# Revit family: Burko F-9000 Pendel
name_source: partatom
category: HLS-Bauteile
units: mm (PartAtom-declared; Revit-internal decimal feet)

## family parameters
Arbeitsebenenbasiert = Nein
Beim Laden mit Abzugskörper schneiden = Nein
Bemaßung runder Anschluss = Durchmesser verwenden
Beschriftungsausrichtung beibehalten = Nein
Gemeinsam genutzt = Nein
Immer vertikal = Ja
Klassifizierung = Keine
Raumberechnungspunkt = Nein
Teiletyp = Normal

## types (5) — shared parameters
Anschluss 1" = 25 mm  [stored 0.082021 ft]
Anschluss 1/2" = 15 mm  [stored 0.0492126 ft]
Datenblatt = https://www.burkhalter-h2o.ch
Homepage = https://www.burkhalter-h2o.ch
LUT = LUT_Burko_F-9000
Sockel_Höhe = 100 mm  [stored 0.328084 ft]
Steuerung_Breite = 200 mm  [stored 0.656168 ft]
Steuerung_Höhe = 175 mm  [stored 0.574147 ft]
Steuerung_Tiefe = 75 mm  [stored 0.246063 ft]
zero-valued in all types: Vorgabe-Ansicht

## per-type parameters (varying)
| type | A | B | Behälterkopf | C | G | Harzinhalt_pro_Harzdruckbehälter | Sockel_Absatz_Oben | Sockel_Absatz_Unten |
| Burko F-9000 - 15L | 208 mm | 940 mm  [stored 3.08399 ft] | 75 mm  [stored 0.246063 ft] | 1070 mm  [stored 3.5105 ft] | 370 mm  [stored 1.21391 ft] | 15L | 84 mm  [stored 0.275591 ft] | 114 mm  [stored 0.374016 ft] |
| Burko F-9000 - 25L | 257 mm  [stored 0.843176 ft] | 940 mm  [stored 3.08399 ft] | 100 mm  [stored 0.328084 ft] | 1070 mm  [stored 3.5105 ft] | 450 mm  [stored 1.47638 ft] | 25L | 109 mm  [stored 0.357612 ft] | 139 mm  [stored 0.456037 ft] |
| Burko F-9000 - 50L | 304 mm  [stored 0.997375 ft] | 1270 mm  [stored 4.16667 ft] | 125 mm  [stored 0.410105 ft] | 1400 mm  [stored 4.59318 ft] | 450 mm  [stored 1.47638 ft] | 50L | 132 mm  [stored 0.433071 ft] | 162 mm  [stored 0.531496 ft] |
| Burko F-9000 - 75L | 369 mm  [stored 1.21063 ft] | 1710 mm  [stored 5.61024 ft] | 125 mm  [stored 0.410105 ft] | 1840 mm  [stored 6.03675 ft] | 650 mm  [stored 2.13255 ft] | 75L | 165 mm | 195 mm  [stored 0.639764 ft] |
| Burko F-9000 - 100L | 406 mm  [stored 1.33202 ft] | 1710 mm  [stored 5.61024 ft] | 150 mm  [stored 0.492126 ft] | 1840 mm  [stored 6.03675 ft] | 650 mm  [stored 2.13255 ft] | 100L | 183 mm | 213 mm  [stored 0.698819 ft] |

note: [stored X ft] marks values corroborated as IEEE doubles in the binary element streams (Revit-internal decimal feet)
